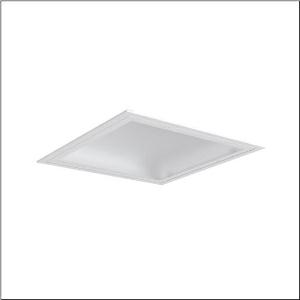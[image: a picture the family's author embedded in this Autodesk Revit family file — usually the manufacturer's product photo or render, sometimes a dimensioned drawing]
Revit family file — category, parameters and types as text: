
# Revit family: mira_21_51fr427a432a
name_source: partatom
category: Lighting Fixtures
units: mm (PartAtom-declared; Revit-internal decimal feet)

## family parameters
Cut with Voids When Loaded = No
Host = Face
Light Source = No
Part Type = Normal
Room Calculation Point = No
Round Connector Dimension = Use Diameter
Shared = No

## types (1)
- Mira 21 (1 x LED, 3220 lm, 23 W, 4000K)
    Apparent Load = 23 VA
    CIE Flux Codes = 50 81 97 100 100
    Color Rendering = 80
    Color Temperature = 4000K
    Default Elevation = 1800 mm
    Description = Mira 21, clean room luminaire, primary light control with reflector, primary optical cover: cover, of PC, light emission: direct distribution, primary light characteristic: symmetric, installation type: recessed, LED, rated luminous flux: 3.220lm, luminous efficacy: 140lm/W, light colour: 840, colour temperature: 4000K, control gear: ON/OFF, with terminal, 3-pole, max. 2.5mm², mains connection: 230V, AC, 50/60Hz, rated input power: 23W, luminaire housing, of sheet steel, coated, pure white (RAL 9010), with concealed spring brackets, module: M625, length: 623mm, width: 623mm, height: 115mm, protection rating (complete): IP54, insulation class (complete): insulation class I (protective earthing), certification: CE, UKCA, permissible operating ambient temperature: -5..+40°C, standard: EN 50419, packaging unit: 1 piece
    Height = 0 mm  [stored 0 ft]
    Lamp = 1 x LED
    Lamp Light Flux = 3220 lm
    Lamp Power = 23 W
    Lamp count = 1
    Length = 625 mm
    Luminous efficacy = 140 lm/W
    Manufacturer = Siteco
    ModVariant = No
    Model = 51FR427A432A
    Mounting Place = Ceiling
    Mounting Type = Recessed
    Number of Poles = 1
    OnlyDefault = Yes
    Power Factor = 1
    Product Name = Mira 21
    Product group = clean room luminaire | ceiling recessed
    ProductGroupID = 402
    Protection Class = Protection class I
    Protection Degree = IP 54
    RLX_Detail_Level = 1
    RLX_Emergency_Light_Flux = 0 lm
    RLX_Emergency_Type = 0
    RLX_Emergency_Type_DB = No
    RlxData = <blob elided: 13377 chars, md5=0027afe7>
    Socket = socket
    Standby Power = 0 W
    System Light Flux = 3220 lm
    System Power = 23 W
    Type Comments = Product without accessories
    Type Image = l_1007109.jpg
    URL = http://relux.com
    VarID = ---
    Voltage = 0 V
    Weight = 0.00 kg
    Width = 625 mm

note: [stored X ft] marks values corroborated as IEEE doubles in the binary element streams (Revit-internal decimal feet)

## geometry (parser evidence)
native form markers: Sweep x10
no freeform markers — native parametric forms only
